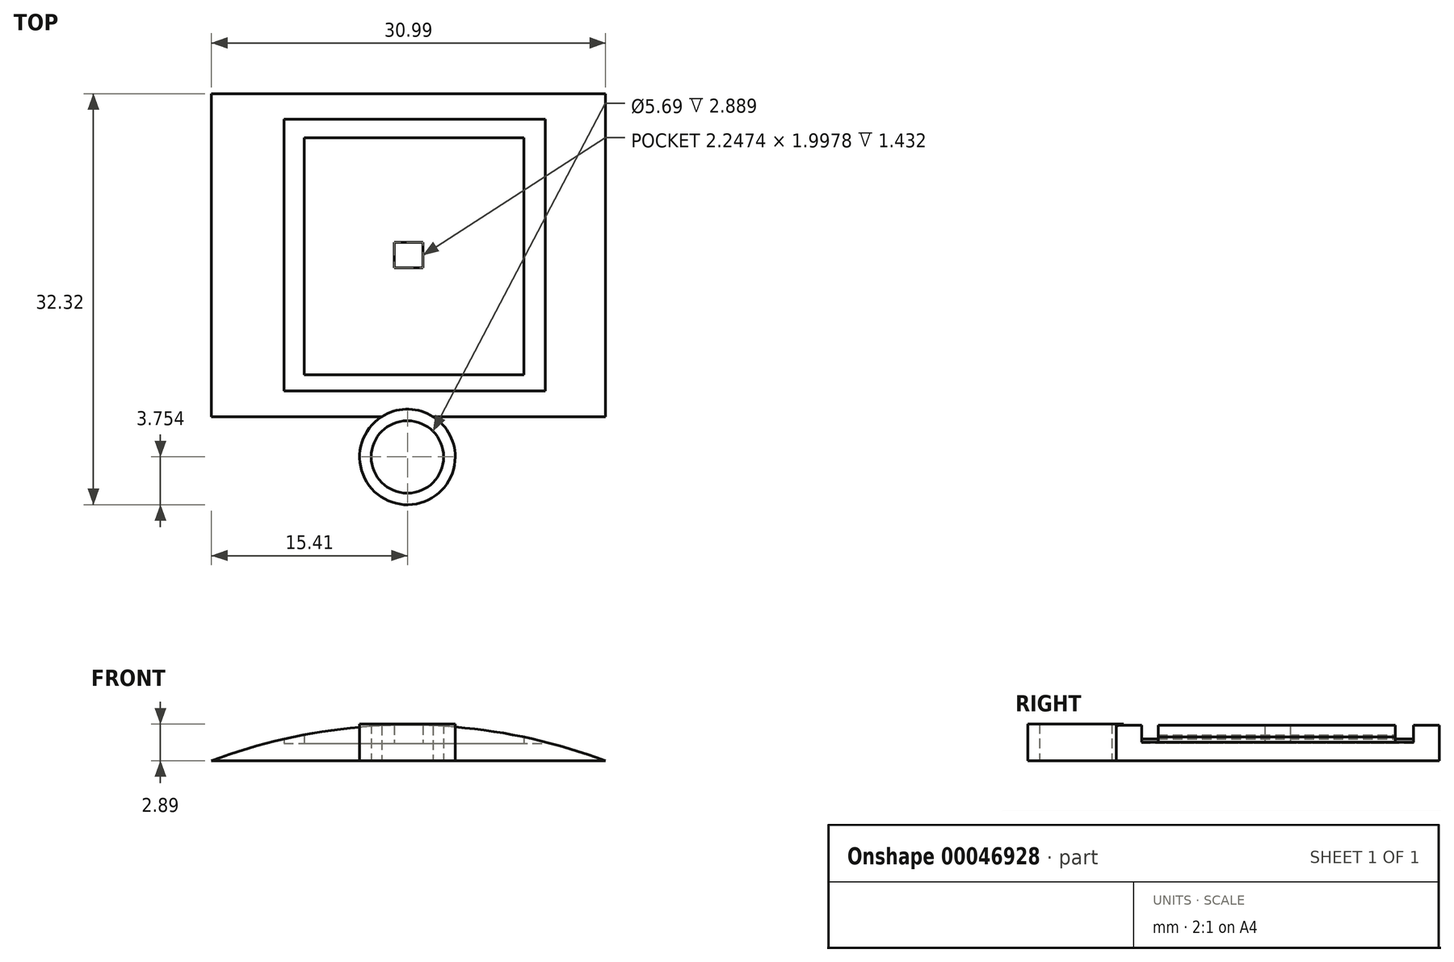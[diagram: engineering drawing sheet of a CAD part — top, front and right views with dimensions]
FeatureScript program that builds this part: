
annotation { "Feature Type Name" : "Feature", "Feature Type Description" : "" }
export const myFeature = defineFeature(function(context is Context, id is Id, definition is map)
    precondition{}
    {
        {
            var Q0;
            Q0=qCreatedBy(makeId("Front.planeOp"),FACE);
            var sketch = newSketch(context, id + "F0", { "sketchPlane" : qUnion([Q0])});
            skLineSegment(sketch, "E0", {"start": v(-15.4, 0) * mm, "end": v(15.58, 0) * mm});
            skLineSegment(sketch, "E1", {"start": v(0, 0) * mm, "end": v(0, 2.8) * mm});
            skArc(sketch, "E2", {"start": v(15.58, 0) * mm, "mid": v(0.09, 2.8) * mm, "end": v(-15.4, 0) * mm});
            skSolve(sketch);
        }
        {
            var Q0;
            Q0 = qSketchRegion(id + "F0", true);
            extrude(context, id + "F1", {"entities" : qUnion([Q0]), "depth" : 12.7 * mm, "hasSecondDirection" : true, "secondDirectionOppositeDirection" : true, "secondDirectionDepth" : 12.7 * mm});
        }
        {
            var Q0;
            Q0=qCreatedBy(makeId("Top.planeOp"),FACE);
            var sketch = newSketch(context, id + "F2", { "sketchPlane" : qUnion([Q0])});
            skCircle(sketch, "E3", {"center": v(0, -15.87) * mm, "radius": 3.76 * mm});
            skCircle(sketch, "E4", {"center": v(0, -15.87) * mm, "radius": 2.85 * mm});
            skSolve(sketch);
        }
        {
            var Q0;
            Q0=makeQuery(id+"F2.imprint","IMPRINT",FACE,{"disambiguationData":[TD([[makeQuery(id+"F2.imprint","IMPRINT",EDGE,{"derivedFrom":sQuery(id+"F2.wireOp",EDGE,"E3")}),1.0]])]});
            extrude(context, id + "F3", {"entities" : qUnion([Q0]), "operationType" : NewBodyOperationType.ADD, "depth" : 2.9 * mm});
        }
        {
            var Q0;
            Q0=qCreatedBy(makeId("Top.planeOp"),FACE);
            var sketch = newSketch(context, id + "F4", { "sketchPlane" : qUnion([Q0])});
            skLineSegment(sketch, "E5.bottom", {"start": v(-9.72, 10.69) * mm, "end": v(10.85, 10.69) * mm});
            skLineSegment(sketch, "E5.top", {"start": v(-9.72, -10.69) * mm, "end": v(10.85, -10.69) * mm});
            skLineSegment(sketch, "E5.left", {"start": v(-9.72, 10.69) * mm, "end": v(-9.72, -10.69) * mm});
            skLineSegment(sketch, "E5.right", {"start": v(10.85, 10.69) * mm, "end": v(10.85, -10.69) * mm});
            skLineSegment(sketch, "E6.bottom", {"start": v(-8.12, 9.24) * mm, "end": v(9.15, 9.24) * mm});
            skLineSegment(sketch, "E6.top", {"start": v(-8.12, -9.39) * mm, "end": v(9.15, -9.39) * mm});
            skLineSegment(sketch, "E6.left", {"start": v(-8.12, 9.24) * mm, "end": v(-8.12, -9.39) * mm});
            skLineSegment(sketch, "E6.right", {"start": v(9.15, 9.24) * mm, "end": v(9.15, -9.39) * mm});
            skLineSegment(sketch, "E7.bottom", {"start": v(-8.12, 1) * mm, "end": v(9.15, 1) * mm});
            skLineSegment(sketch, "E7.top", {"start": v(-8.12, -1) * mm, "end": v(9.15, -1) * mm});
            skLineSegment(sketch, "E7.left", {"start": v(-8.12, 1) * mm, "end": v(-8.12, -1) * mm});
            skLineSegment(sketch, "E7.right", {"start": v(9.15, 1) * mm, "end": v(9.15, -1) * mm});
            skLineSegment(sketch, "E8.bottom", {"start": v(-1.04, 9.24) * mm, "end": v(1.2, 9.24) * mm});
            skLineSegment(sketch, "E8.top", {"start": v(-1.04, -9.39) * mm, "end": v(1.2, -9.39) * mm});
            skLineSegment(sketch, "E8.left", {"start": v(-1.04, 9.24) * mm, "end": v(-1.04, -9.39) * mm});
            skLineSegment(sketch, "E8.right", {"start": v(1.2, 9.24) * mm, "end": v(1.2, -9.39) * mm});
            skSolve(sketch);
        }
        {
            var Q0;
            {var subQ4=sQuery(id+"F4.wireOp",EDGE,"E8.top");Q0=makeQuery(id+"F4.imprint","IMPRINT",FACE,{"disambiguationData":[TD([[makeQuery(id+"F4.imprint","IMPRINT",EDGE,{"derivedFrom":subQ4}),1.0]])]});}
            var Q1;
            {var subQ4=sQuery(id+"F4.wireOp",EDGE,"E8.bottom");Q1=makeQuery(id+"F4.imprint","IMPRINT",FACE,{"disambiguationData":[TD([[makeQuery(id+"F4.imprint","IMPRINT",EDGE,{"derivedFrom":subQ4}),-1.0]])]});}
            var Q2;
            {var subQ0=sQuery(id+"F4.wireOp",EDGE,"E8.left");var subQ3=sQuery(id+"F4.wireOp",EDGE,"E7.bottom");var subQ4=makeQuery(id+"F4.imprint","INTERSECT",VERTEX,{"derivedFrom":[subQ3,subQ0]});Q2=makeQuery(id+"F4.imprint","IMPRINT",FACE,{"disambiguationData":[TD([[makeQuery(id+"F4.imprint","IMPRINT",EDGE,{"disambiguationData":[TD([[subQ4,-1.0]])],"derivedFrom":subQ3}),-1.0]])]});}
            var Q3;
            {var subQ6=sQuery(id+"F4.wireOp",EDGE,"E7.right");Q3=makeQuery(id+"F4.imprint","IMPRINT",FACE,{"disambiguationData":[TD([[makeQuery(id+"F4.imprint","IMPRINT",EDGE,{"derivedFrom":subQ6}),-1.0]])]});}
            var Q4;
            {var subQ5=sQuery(id+"F4.wireOp",EDGE,"E7.left");Q4=makeQuery(id+"F4.imprint","IMPRINT",FACE,{"disambiguationData":[TD([[makeQuery(id+"F4.imprint","IMPRINT",EDGE,{"derivedFrom":subQ5}),1.0]])]});}
            var Q5;
            Q5=makeQuery(id+"F4.imprint","IMPRINT",FACE,{"disambiguationData":[TD([[makeQuery(id+"F4.imprint","IMPRINT",EDGE,{"derivedFrom":sQuery(id+"F4.wireOp",EDGE,"E5.bottom")}),-1.0]])]});
            var Q6;
            Q6=sQuery(id+"F4.wireOp",EDGE,"E8.right");
            extrude(context, id + "F5", {"entities" : qUnion([Q0, Q1, Q2, Q3, Q4, Q5]), "operationType" : NewBodyOperationType.REMOVE, "surfaceEntities" : qUnion([Q6]), "depth" : 3.05 * mm, "hasSecondDirection" : true, "secondDirectionOppositeDirection" : false, "secondDirectionDepth" : 1.36 * mm});
        }
    });
